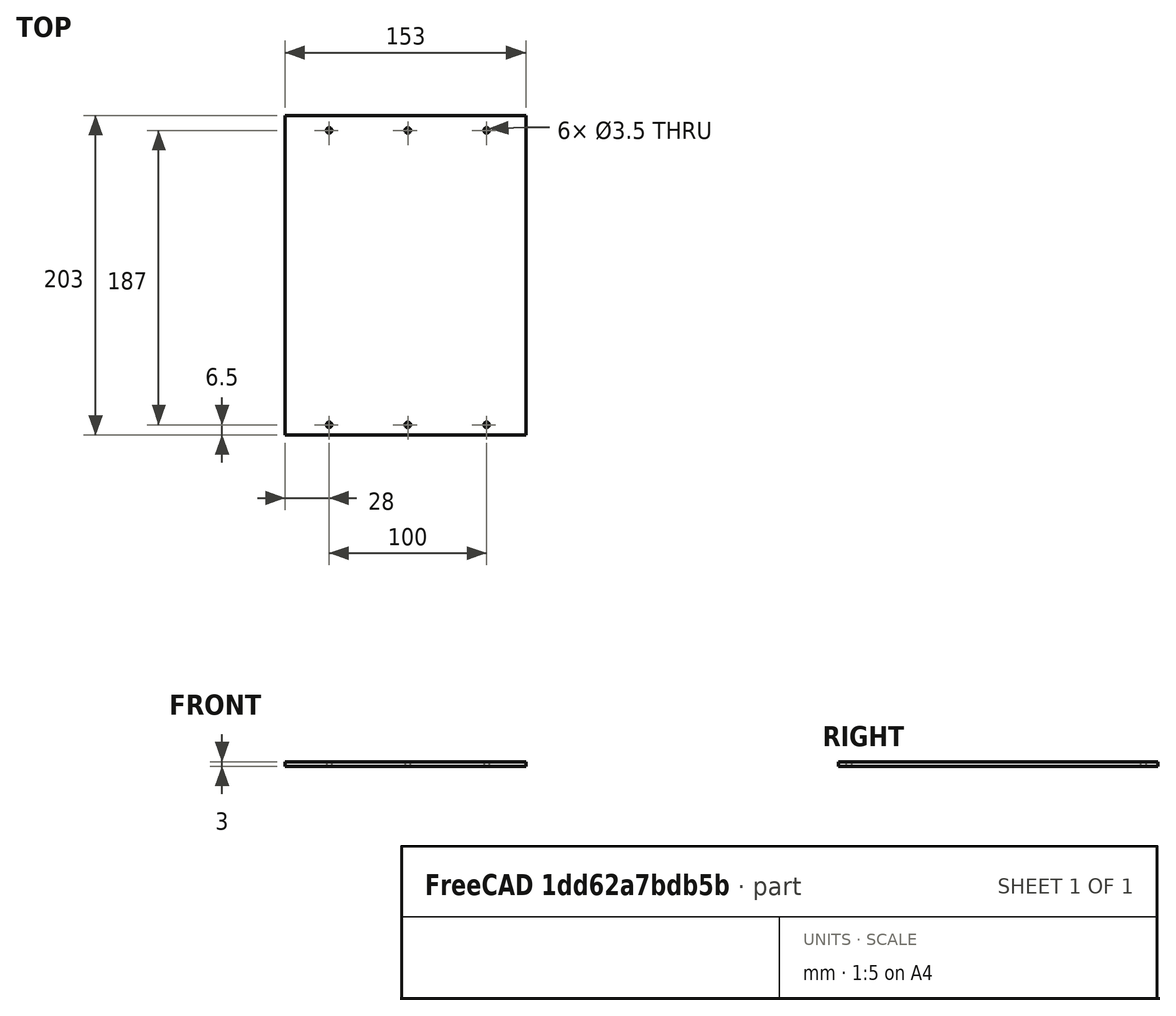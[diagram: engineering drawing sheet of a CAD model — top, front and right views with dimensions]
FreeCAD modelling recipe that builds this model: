
FCSTD DOCUMENT  (FreeCAD 0.21R30398 (Git))
Label: T41_Top_Right_GR01
License: All rights reserved
LicenseURL: http://en.wikipedia.org/wiki/All_rights_reserved
objects: Sketcher::SketchObject×1, PartDesign::Pad×1, PartDesign::Body×1
note: 4 computed .brp shape members not serialized (recipe doc carries the construction recipe); baked Part::Feature solids carry a one-line shape summary decoded from their .brp

FEATURE [Sketcher::SketchObject] Sketch  label="SketchBase"
  FullyConstrained = true
  MapMode = 5
  Support = -> [XY_Plane]
  sketch-geometry (10):
    g0: LineSegment StartX=0 StartY=0 StartZ=0 EndX=-153 EndY=0 EndZ=0
    g1: LineSegment StartX=-153 StartY=0 StartZ=0 EndX=-153 EndY=203 EndZ=0
    g2: LineSegment StartX=-153 StartY=203 StartZ=0 EndX=0 EndY=203 EndZ=0
    g3: LineSegment StartX=0 StartY=203 StartZ=0 EndX=0 EndY=0 EndZ=0
    g4: Circle CenterX=-125 CenterY=193.5 CenterZ=0 NormalX=0 NormalY=0 NormalZ=1 AngleXU=0 Radius=1.75
    g5: Circle CenterX=-125 CenterY=6.5 CenterZ=0 NormalX=0 NormalY=0 NormalZ=1 AngleXU=0 Radius=1.75
    g6: Circle CenterX=-25 CenterY=6.5 CenterZ=0 NormalX=0 NormalY=0 NormalZ=1 AngleXU=0 Radius=1.75
    g7: Circle CenterX=-75 CenterY=6.5 CenterZ=0 NormalX=0 NormalY=0 NormalZ=1 AngleXU=0 Radius=1.75
    g8: Circle CenterX=-25 CenterY=193.5 CenterZ=0 NormalX=0 NormalY=0 NormalZ=1 AngleXU=0 Radius=1.75
    g9: Circle CenterX=-75 CenterY=193.5 CenterZ=0 NormalX=0 NormalY=0 NormalZ=1 AngleXU=0 Radius=1.75
  constraints (29):
    c: Coincident(g0,g1)
    c: Coincident(g1,g2)
    c: Coincident(g2,g3)
    c: Coincident(g3,g0)
    c: Horizontal(g0)
    c: Horizontal(g2)
    c: Vertical(g1)
    c: Vertical(g3)
    c: Coincident(g0,g-1)
    c: DistanceY(g1,g1) = 203
    c: DistanceX(g2,g2) = 153
    c: DistanceX(g4,g0) = 125
    c: DistanceX(g5,g0) = 125
    c: DistanceX(g6,g0) = 25
    c: Diameter(g6) = 3.5
    c: DistanceX(g7,g0) = 75
    c: Diameter(g7) = 3.5
    c: DistanceX(g9,g2) = 75
    c: DistanceX(g8,g2) = 25
    c: Equal(g9,g8)
    c: DistanceY(g4,g1) = 9.5
    c: DistanceY(g0,g5) = 6.5
    c: Horizontal(g5,g7)
    c: Horizontal(g7,g6)
    c: Diameter(g5) = 3.5
    c: DistanceY(g9,g2) = 9.5
    c: DistanceY(g8,g2) = 9.5
    c: Equal(g4,g9)
    c: Diameter(g9) = 3.5
FEATURE [PartDesign::Pad] Pad  label="Base"
  Direction = (0,0,1)
  Length = 3
  Length2 = 100
  Profile = -> Sketch
  Type = 0
FEATURE [PartDesign::Body] Body
  Group = -> [Sketch,Pad]
  Origin = -> Origin
  Tip = -> Pad
